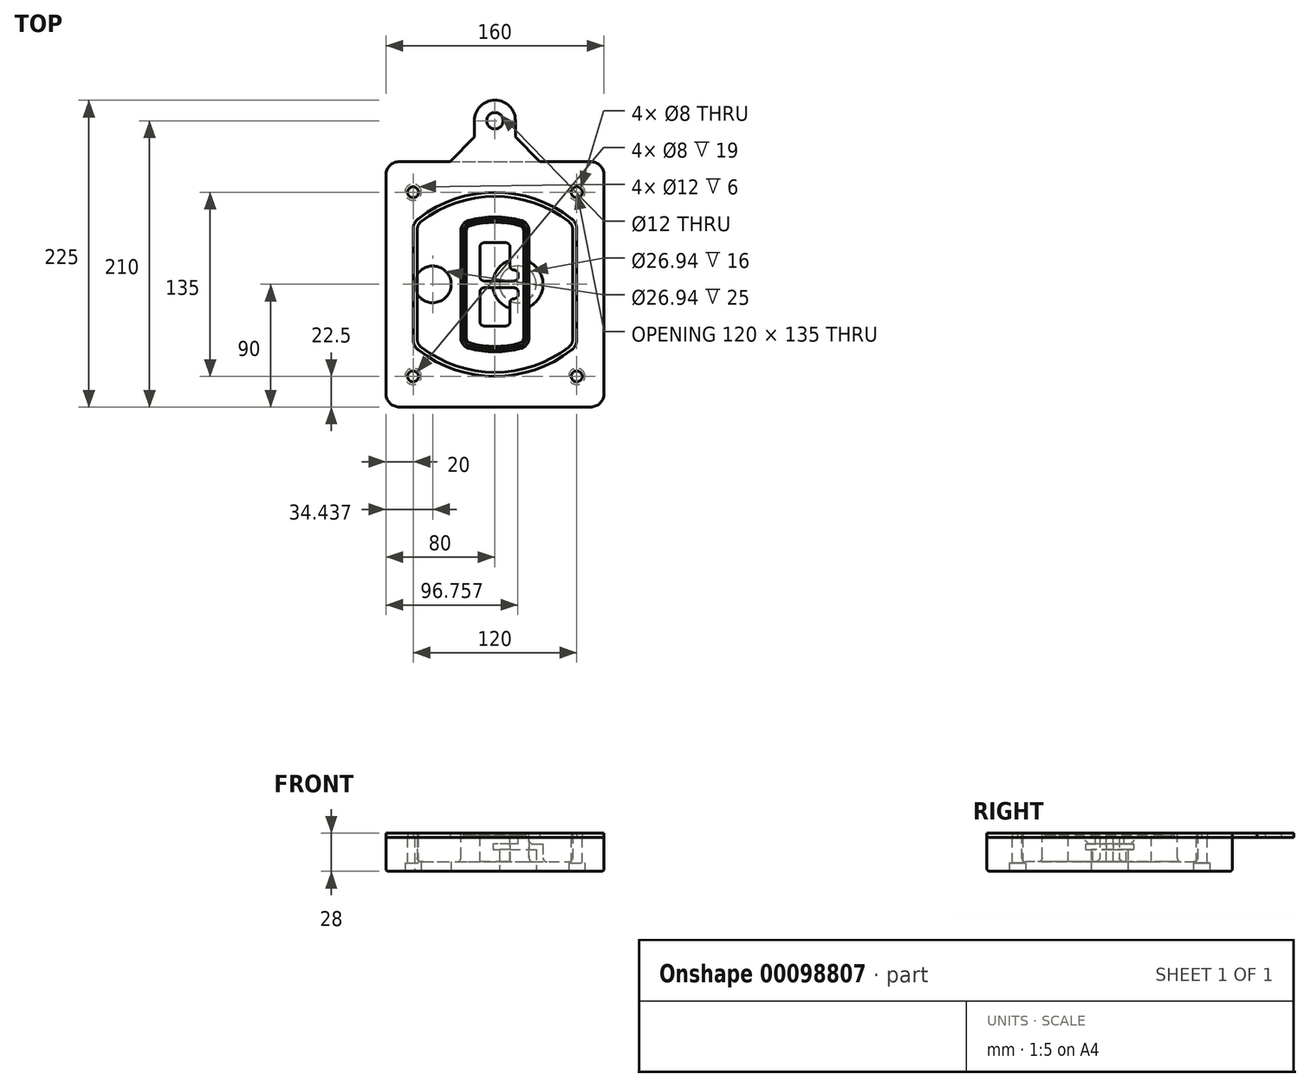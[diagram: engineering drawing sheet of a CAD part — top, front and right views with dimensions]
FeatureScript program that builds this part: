
annotation { "Feature Type Name" : "Feature", "Feature Type Description" : "" }
export const myFeature = defineFeature(function(context is Context, id is Id, definition is map)
    precondition{}
    {
        {
            var Q0;
            Q0=qCreatedBy(makeId("Top.planeOp"),FACE);
            var sketch = newSketch(context, id + "F0", { "sketchPlane" : qUnion([Q0])});
            skPoint(sketch, "E0.rect.middle", {"position": v(0, 0) * mm});
            skLineSegment(sketch, "E1.bottom", {"start": v(-70, -90) * mm, "end": v(70, -90) * mm});
            skLineSegment(sketch, "E1.top", {"start": v(-70, 90) * mm, "end": v(70, 90) * mm});
            skLineSegment(sketch, "E1.left", {"start": v(-80, -80) * mm, "end": v(-80, 80) * mm});
            skLineSegment(sketch, "E1.right", {"start": v(80, -80) * mm, "end": v(80, 80) * mm});
            skLineSegment(sketch, "E2", {"start": v(-80, 90) * mm, "end": v(80, -90) * mm, "construction": true});
            skLineSegment(sketch, "E3", {"start": v(80, 90) * mm, "end": v(-80, -90) * mm, "construction": true});
            skCircle(sketch, "E4", {"center": v(-60, 67.5) * mm, "radius": 4 * mm});
            skCircle(sketch, "E5", {"center": v(60, 67.5) * mm, "radius": 4 * mm});
            skCircle(sketch, "E6", {"center": v(60, -67.5) * mm, "radius": 4 * mm});
            skCircle(sketch, "E7", {"center": v(-60, -67.5) * mm, "radius": 4 * mm});
            skLineSegment(sketch, "E8", {"start": v(-60, 67.5) * mm, "end": v(60, 67.5) * mm, "construction": true});
            skLineSegment(sketch, "E9", {"start": v(60, 67.5) * mm, "end": v(60, -67.5) * mm, "construction": true});
            skLineSegment(sketch, "E10", {"start": v(60, -67.5) * mm, "end": v(-60, -67.5) * mm, "construction": true});
            skLineSegment(sketch, "E11", {"start": v(-60, -67.5) * mm, "end": v(-60, 67.5) * mm, "construction": true});
            skLineSegment(sketch, "E12", {"start": v(-60, 40.3) * mm, "end": v(-60, -40.3) * mm});
            skLineSegment(sketch, "E13", {"start": v(60, 40.3) * mm, "end": v(60, -40.3) * mm});
            skArc(sketch, "E14", {"start": v(56.15, 48.18) * mm, "mid": v(0, 67.5) * mm, "end": v(-56.15, 48.18) * mm});
            skArc(sketch, "E15", {"start": v(-56.15, -48.18) * mm, "mid": v(0, -67.5) * mm, "end": v(56.15, -48.18) * mm});
            skLineSegment(sketch, "E16", {"start": v(-60, 0) * mm, "end": v(60, 0) * mm, "construction": true});
            skPoint(sketch, "E17.visualSharp", {"position": v(-60, -45) * mm});
            skArc(sketch, "E17.filletArc", {"start": v(-60, -40.3) * mm, "mid": v(-58.99, -44.68) * mm, "end": v(-56.15, -48.18) * mm});
            skPoint(sketch, "E18.visualSharp", {"position": v(-60, 45) * mm});
            skArc(sketch, "E18.filletArc", {"start": v(-56.15, 48.18) * mm, "mid": v(-58.99, 44.68) * mm, "end": v(-60, 40.3) * mm});
            skPoint(sketch, "E19.visualSharp", {"position": v(60, 45) * mm});
            skArc(sketch, "E19.filletArc", {"start": v(60, 40.3) * mm, "mid": v(58.99, 44.68) * mm, "end": v(56.15, 48.18) * mm});
            skPoint(sketch, "E20.visualSharp", {"position": v(60, -45) * mm});
            skArc(sketch, "E20.filletArc", {"start": v(56.15, -48.18) * mm, "mid": v(58.99, -44.68) * mm, "end": v(60, -40.3) * mm});
            skPoint(sketch, "E21.visualSharp", {"position": v(-80, 90) * mm});
            skArc(sketch, "E21.filletArc", {"start": v(-70, 90) * mm, "mid": v(-77.07, 87.07) * mm, "end": v(-80, 80) * mm});
            skPoint(sketch, "E22.visualSharp", {"position": v(80, 90) * mm});
            skArc(sketch, "E22.filletArc", {"start": v(80, 80) * mm, "mid": v(77.07, 87.07) * mm, "end": v(70, 90) * mm});
            skPoint(sketch, "E23.visualSharp", {"position": v(80, -90) * mm});
            skArc(sketch, "E23.filletArc", {"start": v(70, -90) * mm, "mid": v(77.07, -87.07) * mm, "end": v(80, -80) * mm});
            skPoint(sketch, "E24.visualSharp", {"position": v(-80, -90) * mm});
            skArc(sketch, "E24.filletArc", {"start": v(-80, -80) * mm, "mid": v(-77.07, -87.07) * mm, "end": v(-70, -90) * mm});
            skArc(sketch, "E25.0", {"start": v(57, 40.3) * mm, "mid": v(56.3, 43.36) * mm, "end": v(54.3, 45.81) * mm});
            skLineSegment(sketch, "E25.1", {"start": v(57, 40.3) * mm, "end": v(57, -40.3) * mm});
            skArc(sketch, "E25.2", {"start": v(54.3, -45.81) * mm, "mid": v(56.3, -43.36) * mm, "end": v(57, -40.3) * mm});
            skArc(sketch, "E25.3", {"start": v(-54.3, -45.81) * mm, "mid": v(0, -64.5) * mm, "end": v(54.3, -45.81) * mm});
            skArc(sketch, "E25.4", {"start": v(-57, -40.3) * mm, "mid": v(-56.3, -43.36) * mm, "end": v(-54.3, -45.81) * mm});
            skArc(sketch, "E25.5", {"start": v(54.3, 45.81) * mm, "mid": v(0, 64.5) * mm, "end": v(-54.3, 45.81) * mm});
            skLineSegment(sketch, "E25.6", {"start": v(-57, 40.3) * mm, "end": v(-57, -40.3) * mm});
            skArc(sketch, "E25.7", {"start": v(-54.3, 45.81) * mm, "mid": v(-56.3, 43.36) * mm, "end": v(-57, 40.3) * mm});
            skArc(sketch, "E26.0", {"start": v(-58.62, 51.33) * mm, "mid": v(-62.58, 46.43) * mm, "end": v(-64, 40.3) * mm});
            skArc(sketch, "E26.1", {"start": v(58.62, 51.33) * mm, "mid": v(0, 71.5) * mm, "end": v(-58.62, 51.33) * mm});
            skArc(sketch, "E26.2", {"start": v(64, 40.3) * mm, "mid": v(62.58, 46.43) * mm, "end": v(58.62, 51.33) * mm});
            skLineSegment(sketch, "E26.3", {"start": v(64, 40.3) * mm, "end": v(64, -40.3) * mm});
            skArc(sketch, "E26.4", {"start": v(58.62, -51.33) * mm, "mid": v(62.58, -46.43) * mm, "end": v(64, -40.3) * mm});
            skLineSegment(sketch, "E26.5", {"start": v(-64, 40.3) * mm, "end": v(-64, -40.3) * mm});
            skArc(sketch, "E26.6", {"start": v(-58.62, -51.33) * mm, "mid": v(0, -71.5) * mm, "end": v(58.62, -51.33) * mm});
            skArc(sketch, "E26.7", {"start": v(-64, -40.3) * mm, "mid": v(-62.58, -46.43) * mm, "end": v(-58.62, -51.33) * mm});
            skSolve(sketch);
        }
        {
            var Q0;
            Q0=makeQuery(id+"F0.imprint","IMPRINT",FACE,{"disambiguationData":[TD([[makeQuery(id+"F0.imprint","IMPRINT",EDGE,{"derivedFrom":sQuery(id+"F0.wireOp",EDGE,"E1.bottom")}),1.0]])]});
            var Q1;
            Q1=makeQuery(id+"F0.imprint","IMPRINT",FACE,{"disambiguationData":[TD([[makeQuery(id+"F0.imprint","IMPRINT",EDGE,{"derivedFrom":sQuery(id+"F0.wireOp",EDGE,"E12")}),1.0]])]});
            var Q2;
            Q2=makeQuery(id+"F0.imprint","IMPRINT",FACE,{"disambiguationData":[TD([[makeQuery(id+"F0.imprint","IMPRINT",EDGE,{"derivedFrom":sQuery(id+"F0.wireOp",EDGE,"E25.0")}),1.0]])]});
            var Q3;
            Q3=makeQuery(id+"F0.imprint","IMPRINT",FACE,{"disambiguationData":[TD([[makeQuery(id+"F0.imprint","IMPRINT",EDGE,{"derivedFrom":sQuery(id+"F0.wireOp",EDGE,"E12")}),-1.0]])]});
            extrude(context, id + "F1", {"entities" : qUnion([Q0, Q1, Q2, Q3]), "oppositeDirection" : true, "depth" : 25 * mm});
        }
        {
            var Q0;
            Q0=makeQuery(id+"F0.imprint","IMPRINT",FACE,{"disambiguationData":[TD([[makeQuery(id+"F0.imprint","IMPRINT",EDGE,{"derivedFrom":sQuery(id+"F0.wireOp",EDGE,"E12")}),1.0]])]});
            extrude(context, id + "F2", {"entities" : qUnion([Q0]), "operationType" : NewBodyOperationType.ADD, "depth" : 3 * mm});
        }
        {
            var Q0;
            Q0=makeQuery(id+"F0.imprint","IMPRINT",FACE,{"disambiguationData":[TD([[makeQuery(id+"F0.imprint","IMPRINT",EDGE,{"derivedFrom":sQuery(id+"F0.wireOp",EDGE,"E25.0")}),1.0]])]});
            extrude(context, id + "F3", {"entities" : qUnion([Q0]), "operationType" : NewBodyOperationType.REMOVE, "oppositeDirection" : true, "depth" : 18 * mm});
        }
        {
            var Q0;
            Q0=makeQuery(id+"F2.opExtrude","CAP_FACE",FACE,{"disambiguationData":[OSD([sQuery(id+"F0.wireOp",EDGE,"E12"),sQuery(id+"F0.wireOp",EDGE,"E13"),sQuery(id+"F0.wireOp",EDGE,"E14"),sQuery(id+"F0.wireOp",EDGE,"E15"),sQuery(id+"F0.wireOp",EDGE,"E17.filletArc"),sQuery(id+"F0.wireOp",EDGE,"E18.filletArc"),sQuery(id+"F0.wireOp",EDGE,"E19.filletArc"),sQuery(id+"F0.wireOp",EDGE,"E20.filletArc"),sQuery(id+"F0.wireOp",EDGE,"E25.0"),sQuery(id+"F0.wireOp",EDGE,"E25.1"),sQuery(id+"F0.wireOp",EDGE,"E25.2"),sQuery(id+"F0.wireOp",EDGE,"E25.3"),sQuery(id+"F0.wireOp",EDGE,"E25.4"),sQuery(id+"F0.wireOp",EDGE,"E25.5"),sQuery(id+"F0.wireOp",EDGE,"E25.6"),sQuery(id+"F0.wireOp",EDGE,"E25.7")])],"isStart":false});
            var sketch = newSketch(context, id + "F4", { "sketchPlane" : qUnion([Q0])});
            skArc(sketch, "E27.0", {"start": v(-19.08, -46.97) * mm, "mid": v(0, -49.5) * mm, "end": v(19.08, -46.97) * mm});
            skArc(sketch, "E28.0", {"start": v(19.08, 46.97) * mm, "mid": v(0, 49.5) * mm, "end": v(-19.08, 46.97) * mm});
            skLineSegment(sketch, "E29", {"start": v(-25, 39.25) * mm, "end": v(-25, -39.25) * mm});
            skLineSegment(sketch, "E30", {"start": v(25, 39.25) * mm, "end": v(25, -39.25) * mm});
            skLineSegment(sketch, "E31", {"start": v(-25, 45.1) * mm, "end": v(25, 45.1) * mm, "construction": true});
            skLineSegment(sketch, "E32", {"start": v(-25, -45.1) * mm, "end": v(25, -45.1) * mm, "construction": true});
            skPoint(sketch, "E33.visualSharp", {"position": v(-25, 45.1) * mm});
            skArc(sketch, "E33.filletArc", {"start": v(-19.08, 46.97) * mm, "mid": v(-23.35, 44.11) * mm, "end": v(-25, 39.25) * mm});
            skPoint(sketch, "E34.visualSharp", {"position": v(25, 45.1) * mm});
            skArc(sketch, "E34.filletArc", {"start": v(25, 39.25) * mm, "mid": v(23.35, 44.11) * mm, "end": v(19.08, 46.97) * mm});
            skPoint(sketch, "E35.visualSharp", {"position": v(25, -45.1) * mm});
            skArc(sketch, "E35.filletArc", {"start": v(19.08, -46.97) * mm, "mid": v(23.35, -44.11) * mm, "end": v(25, -39.25) * mm});
            skPoint(sketch, "E36.visualSharp", {"position": v(-25, -45.1) * mm});
            skArc(sketch, "E36.filletArc", {"start": v(-25, -39.25) * mm, "mid": v(-23.35, -44.11) * mm, "end": v(-19.08, -46.97) * mm});
            skArc(sketch, "E37.0", {"start": v(54.3, 45.81) * mm, "mid": v(0, 64.5) * mm, "end": v(-54.3, 45.81) * mm});
            skArc(sketch, "E37.1", {"start": v(-54.3, 45.81) * mm, "mid": v(-56.3, 43.36) * mm, "end": v(-57, 40.3) * mm});
            skLineSegment(sketch, "E37.2", {"start": v(-57, 40.3) * mm, "end": v(-57, -40.3) * mm});
            skArc(sketch, "E37.3", {"start": v(-57, -40.3) * mm, "mid": v(-56.3, -43.36) * mm, "end": v(-54.3, -45.81) * mm});
            skArc(sketch, "E37.4", {"start": v(-54.3, -45.81) * mm, "mid": v(0, -64.5) * mm, "end": v(54.3, -45.81) * mm});
            skArc(sketch, "E37.5", {"start": v(54.3, -45.81) * mm, "mid": v(56.3, -43.36) * mm, "end": v(57, -40.3) * mm});
            skLineSegment(sketch, "E37.6", {"start": v(57, 40.3) * mm, "end": v(57, -40.3) * mm});
            skArc(sketch, "E37.7", {"start": v(57, 40.3) * mm, "mid": v(56.3, 43.36) * mm, "end": v(54.3, 45.81) * mm});
            skLineSegment(sketch, "E38.0", {"start": v(23, 39.25) * mm, "end": v(23, -39.25) * mm});
            skArc(sketch, "E38.1", {"start": v(18.56, -45.04) * mm, "mid": v(21.76, -42.9) * mm, "end": v(23, -39.25) * mm});
            skArc(sketch, "E38.2", {"start": v(-18.56, -45.04) * mm, "mid": v(0, -47.5) * mm, "end": v(18.56, -45.04) * mm});
            skArc(sketch, "E38.3", {"start": v(-23, -39.25) * mm, "mid": v(-21.76, -42.9) * mm, "end": v(-18.56, -45.04) * mm});
            skLineSegment(sketch, "E38.4", {"start": v(-23, 39.25) * mm, "end": v(-23, -39.25) * mm});
            skArc(sketch, "E38.5", {"start": v(23, 39.25) * mm, "mid": v(21.76, 42.9) * mm, "end": v(18.56, 45.04) * mm});
            skArc(sketch, "E38.6", {"start": v(-18.56, 45.04) * mm, "mid": v(-21.76, 42.9) * mm, "end": v(-23, 39.25) * mm});
            skArc(sketch, "E38.7", {"start": v(18.56, 45.04) * mm, "mid": v(0, 47.5) * mm, "end": v(-18.56, 45.04) * mm});
            skArc(sketch, "E39.0", {"start": v(21, 39.25) * mm, "mid": v(20.18, 41.68) * mm, "end": v(18.04, 43.1) * mm});
            skLineSegment(sketch, "E39.1", {"start": v(21, 39.25) * mm, "end": v(21, -39.25) * mm});
            skArc(sketch, "E39.2", {"start": v(18.04, -43.1) * mm, "mid": v(20.18, -41.68) * mm, "end": v(21, -39.25) * mm});
            skArc(sketch, "E39.3", {"start": v(-18.04, -43.1) * mm, "mid": v(0, -45.5) * mm, "end": v(18.04, -43.1) * mm});
            skArc(sketch, "E39.4", {"start": v(-21, -39.25) * mm, "mid": v(-20.18, -41.68) * mm, "end": v(-18.04, -43.1) * mm});
            skArc(sketch, "E39.5", {"start": v(18.04, 43.1) * mm, "mid": v(0, 45.5) * mm, "end": v(-18.04, 43.1) * mm});
            skLineSegment(sketch, "E39.6", {"start": v(-21, 39.25) * mm, "end": v(-21, -39.25) * mm});
            skArc(sketch, "E39.7", {"start": v(-18.04, 43.1) * mm, "mid": v(-20.18, 41.68) * mm, "end": v(-21, 39.25) * mm});
            skLineSegment(sketch, "E40", {"start": v(-25, 0) * mm, "end": v(25, 0) * mm, "construction": true});
            skLineSegment(sketch, "E41", {"start": v(-11, 5.5) * mm, "end": v(-11, 27.5) * mm});
            skLineSegment(sketch, "E42", {"start": v(-8, 30.5) * mm, "end": v(8, 30.5) * mm});
            skLineSegment(sketch, "E43", {"start": v(11, 27.5) * mm, "end": v(11, 13.5) * mm});
            skLineSegment(sketch, "E44", {"start": v(14, 10.5) * mm, "end": v(14, 10.5) * mm});
            skLineSegment(sketch, "E45", {"start": v(17, 7.5) * mm, "end": v(17, 5.5) * mm});
            skLineSegment(sketch, "E46", {"start": v(14, 2.5) * mm, "end": v(-8, 2.5) * mm});
            skPoint(sketch, "E47.visualSharp", {"position": v(-11, 30.5) * mm});
            skArc(sketch, "E47.filletArc", {"start": v(-8, 30.5) * mm, "mid": v(-10.12, 29.62) * mm, "end": v(-11, 27.5) * mm});
            skPoint(sketch, "E48.visualSharp", {"position": v(11, 30.5) * mm});
            skArc(sketch, "E48.filletArc", {"start": v(11, 27.5) * mm, "mid": v(10.12, 29.62) * mm, "end": v(8, 30.5) * mm});
            skPoint(sketch, "E49.visualSharp", {"position": v(11, 10.5) * mm});
            skArc(sketch, "E49.filletArc", {"start": v(11, 13.5) * mm, "mid": v(11.88, 11.38) * mm, "end": v(14, 10.5) * mm});
            skPoint(sketch, "E50.visualSharp", {"position": v(17, 10.5) * mm});
            skArc(sketch, "E50.filletArc", {"start": v(17, 7.5) * mm, "mid": v(16.12, 9.62) * mm, "end": v(14, 10.5) * mm});
            skPoint(sketch, "E51.visualSharp", {"position": v(17, 2.5) * mm});
            skArc(sketch, "E51.filletArc", {"start": v(14, 2.5) * mm, "mid": v(16.12, 3.38) * mm, "end": v(17, 5.5) * mm});
            skPoint(sketch, "E52.visualSharp", {"position": v(-11, 2.5) * mm});
            skArc(sketch, "E52.filletArc", {"start": v(-11, 5.5) * mm, "mid": v(-10.12, 3.38) * mm, "end": v(-8, 2.5) * mm});
            skLineSegment(sketch, "E53.0.MirrorCS", {"start": v(14, -2.5) * mm, "end": v(-8, -2.5) * mm});
            skArc(sketch, "E54.0.MirrorCS", {"start": v(-11, -5.5) * mm, "mid": v(-10.12, -3.38) * mm, "end": v(-8, -2.5) * mm});
            skLineSegment(sketch, "E55.0.MirrorCS", {"start": v(-11, -5.5) * mm, "end": v(-11, -27.5) * mm});
            skArc(sketch, "E56.0.MirrorCS", {"start": v(-8, -30.5) * mm, "mid": v(-10.12, -29.62) * mm, "end": v(-11, -27.5) * mm});
            skLineSegment(sketch, "E57.0.MirrorCS", {"start": v(-8, -30.5) * mm, "end": v(8, -30.5) * mm});
            skArc(sketch, "E58.0.MirrorCS", {"start": v(11, -27.5) * mm, "mid": v(10.12, -29.62) * mm, "end": v(8, -30.5) * mm});
            skLineSegment(sketch, "E59.0.MirrorCS", {"start": v(11, -27.5) * mm, "end": v(11, -13.5) * mm});
            skArc(sketch, "E60.0.MirrorCS", {"start": v(11, -13.5) * mm, "mid": v(11.88, -11.38) * mm, "end": v(14, -10.5) * mm});
            skArc(sketch, "E61.0.MirrorCS", {"start": v(17, -7.5) * mm, "mid": v(16.12, -9.62) * mm, "end": v(14, -10.5) * mm});
            skLineSegment(sketch, "E62.0.MirrorCS", {"start": v(17, -7.5) * mm, "end": v(17, -5.5) * mm});
            skArc(sketch, "E63.0.MirrorCS", {"start": v(14, -2.5) * mm, "mid": v(16.12, -3.38) * mm, "end": v(17, -5.5) * mm});
            skSolve(sketch);
        }
        {
            var Q0;
            Q0=makeQuery(id+"F4.imprint","IMPRINT",FACE,{"disambiguationData":[TD([[makeQuery(id+"F4.imprint","IMPRINT",EDGE,{"derivedFrom":sQuery(id+"F4.wireOp",EDGE,"E27.0")}),1.0]])]});
            var Q1;
            Q1=makeQuery(id+"F4.imprint","IMPRINT",FACE,{"disambiguationData":[TD([[makeQuery(id+"F4.imprint","IMPRINT",EDGE,{"derivedFrom":sQuery(id+"F4.wireOp",EDGE,"E38.0")}),-1.0]])]});
            var Q2;
            Q2=makeQuery(id+"F4.imprint","IMPRINT",FACE,{"disambiguationData":[TD([[makeQuery(id+"F4.imprint","IMPRINT",EDGE,{"derivedFrom":sQuery(id+"F4.wireOp",EDGE,"E39.0")}),1.0]])]});
            extrude(context, id + "F5", {"entities" : qUnion([Q0, Q1, Q2]), "operationType" : NewBodyOperationType.ADD, "endBound" : BoundingType.UP_TO_NEXT, "oppositeDirection" : true, "depth" : 25 * mm});
        }
        {
            var Q0;
            Q0=makeQuery(id+"F4.imprint","IMPRINT",FACE,{"disambiguationData":[TD([[makeQuery(id+"F4.imprint","IMPRINT",EDGE,{"derivedFrom":sQuery(id+"F4.wireOp",EDGE,"E38.0")}),-1.0]])]});
            extrude(context, id + "F6", {"entities" : qUnion([Q0]), "operationType" : NewBodyOperationType.REMOVE, "oppositeDirection" : true, "depth" : 2 * mm});
        }
        {
            var Q0;
            Q0=makeQuery(id+"F1.opExtrude","CAP_FACE",FACE,{"disambiguationData":[OSD([sQuery(id+"F0.wireOp",EDGE,"E1.bottom"),sQuery(id+"F0.wireOp",EDGE,"E1.top"),sQuery(id+"F0.wireOp",EDGE,"E1.left"),sQuery(id+"F0.wireOp",EDGE,"E1.right"),sQuery(id+"F0.wireOp",EDGE,"E4"),sQuery(id+"F0.wireOp",EDGE,"E5"),sQuery(id+"F0.wireOp",EDGE,"E6"),sQuery(id+"F0.wireOp",EDGE,"E7"),sQuery(id+"F0.wireOp",EDGE,"E21.filletArc"),sQuery(id+"F0.wireOp",EDGE,"E22.filletArc"),sQuery(id+"F0.wireOp",EDGE,"E23.filletArc"),sQuery(id+"F0.wireOp",EDGE,"E24.filletArc")])],"isStart":false});
            var sketch = newSketch(context, id + "F7", { "sketchPlane" : qUnion([Q0])});
            skCircle(sketch, "E64", {"center": v(16.76, 0) * mm, "radius": 13.47 * mm});
            skCircle(sketch, "E65", {"center": v(-45.56, 0) * mm, "radius": 13.47 * mm});
            skLineSegment(sketch, "E66", {"start": v(80, 0) * mm, "end": v(-80, 0) * mm});
            skCircle(sketch, "E67", {"center": v(16.76, 0) * mm, "radius": 18.47 * mm});
            skCircle(sketch, "E68", {"center": v(60, -67.5) * mm, "radius": 6 * mm});
            skCircle(sketch, "E69", {"center": v(-60, -67.5) * mm, "radius": 6 * mm});
            skCircle(sketch, "E70", {"center": v(-60, 67.5) * mm, "radius": 6 * mm});
            skCircle(sketch, "E71", {"center": v(60, 67.5) * mm, "radius": 6 * mm});
            skSolve(sketch);
        }
        {
            var Q0;
            {var subQ1=sQuery(id+"F7.wireOp",EDGE,"E66");var subQ4=sQuery(id+"F7.wireOp",EDGE,"E64");var subQ6=makeQuery(id+"F7.imprint","INTERSECT",VERTEX,{"disambiguationData":[OD(0.0)],"derivedFrom":[subQ4,subQ1]});Q0=makeQuery(id+"F7.imprint","IMPRINT",FACE,{"disambiguationData":[TD([[makeQuery(id+"F7.imprint","IMPRINT",EDGE,{"disambiguationData":[TD([[subQ6,-1.0]])],"derivedFrom":subQ4}),-1.0]])]});}
            var Q1;
            {var subQ0=sQuery(id+"F7.wireOp",EDGE,"E66");var subQ1=sQuery(id+"F7.wireOp",EDGE,"E64");var subQ3=makeQuery(id+"F7.imprint","INTERSECT",VERTEX,{"disambiguationData":[OD(0.0)],"derivedFrom":[subQ1,subQ0]});Q1=makeQuery(id+"F7.imprint","IMPRINT",FACE,{"disambiguationData":[TD([[makeQuery(id+"F7.imprint","IMPRINT",EDGE,{"disambiguationData":[TD([[subQ3,-1.0]])],"derivedFrom":subQ1}),1.0]])]});}
            var Q2;
            {var subQ0=sQuery(id+"F7.wireOp",EDGE,"E66");var subQ1=sQuery(id+"F7.wireOp",EDGE,"E64");var subQ3=makeQuery(id+"F7.imprint","INTERSECT",VERTEX,{"disambiguationData":[OD(0.0)],"derivedFrom":[subQ1,subQ0]});Q2=makeQuery(id+"F7.imprint","IMPRINT",FACE,{"disambiguationData":[TD([[makeQuery(id+"F7.imprint","IMPRINT",EDGE,{"disambiguationData":[TD([[subQ3,1.0]])],"derivedFrom":subQ1}),1.0]])]});}
            var Q3;
            {var subQ1=sQuery(id+"F7.wireOp",EDGE,"E66");var subQ4=sQuery(id+"F7.wireOp",EDGE,"E64");var subQ6=makeQuery(id+"F7.imprint","INTERSECT",VERTEX,{"disambiguationData":[OD(0.0)],"derivedFrom":[subQ4,subQ1]});Q3=makeQuery(id+"F7.imprint","IMPRINT",FACE,{"disambiguationData":[TD([[makeQuery(id+"F7.imprint","IMPRINT",EDGE,{"disambiguationData":[TD([[subQ6,1.0]])],"derivedFrom":subQ4}),-1.0]])]});}
            extrude(context, id + "F8", {"entities" : qUnion([Q0, Q1, Q2, Q3]), "operationType" : NewBodyOperationType.ADD, "oppositeDirection" : true, "depth" : 20 * mm});
        }
        {
            var Q0;
            {var subQ0=sQuery(id+"F7.wireOp",EDGE,"E66");var subQ1=sQuery(id+"F7.wireOp",EDGE,"E64");var subQ3=makeQuery(id+"F7.imprint","INTERSECT",VERTEX,{"disambiguationData":[OD(0.0)],"derivedFrom":[subQ1,subQ0]});Q0=makeQuery(id+"F7.imprint","IMPRINT",FACE,{"disambiguationData":[TD([[makeQuery(id+"F7.imprint","IMPRINT",EDGE,{"disambiguationData":[TD([[subQ3,-1.0]])],"derivedFrom":subQ1}),1.0]])]});}
            var Q1;
            {var subQ0=sQuery(id+"F7.wireOp",EDGE,"E66");var subQ1=sQuery(id+"F7.wireOp",EDGE,"E64");var subQ3=makeQuery(id+"F7.imprint","INTERSECT",VERTEX,{"disambiguationData":[OD(0.0)],"derivedFrom":[subQ1,subQ0]});Q1=makeQuery(id+"F7.imprint","IMPRINT",FACE,{"disambiguationData":[TD([[makeQuery(id+"F7.imprint","IMPRINT",EDGE,{"disambiguationData":[TD([[subQ3,1.0]])],"derivedFrom":subQ1}),1.0]])]});}
            extrude(context, id + "F9", {"entities" : qUnion([Q0, Q1]), "operationType" : NewBodyOperationType.REMOVE, "oppositeDirection" : true, "depth" : 16 * mm});
        }
        {
            var Q0;
            {var subQ0=sQuery(id+"F7.wireOp",EDGE,"E66");var subQ1=sQuery(id+"F7.wireOp",EDGE,"E65");var subQ3=makeQuery(id+"F7.imprint","INTERSECT",VERTEX,{"disambiguationData":[OD(0.0)],"derivedFrom":[subQ1,subQ0]});Q0=makeQuery(id+"F7.imprint","IMPRINT",FACE,{"disambiguationData":[TD([[makeQuery(id+"F7.imprint","IMPRINT",EDGE,{"disambiguationData":[TD([[subQ3,-1.0]])],"derivedFrom":subQ1}),1.0]])]});}
            var Q1;
            {var subQ0=sQuery(id+"F7.wireOp",EDGE,"E66");var subQ1=sQuery(id+"F7.wireOp",EDGE,"E65");var subQ3=makeQuery(id+"F7.imprint","INTERSECT",VERTEX,{"disambiguationData":[OD(0.0)],"derivedFrom":[subQ1,subQ0]});Q1=makeQuery(id+"F7.imprint","IMPRINT",FACE,{"disambiguationData":[TD([[makeQuery(id+"F7.imprint","IMPRINT",EDGE,{"disambiguationData":[TD([[subQ3,1.0]])],"derivedFrom":subQ1}),1.0]])]});}
            extrude(context, id + "F10", {"entities" : qUnion([Q0, Q1]), "operationType" : NewBodyOperationType.REMOVE, "oppositeDirection" : true, "depth" : 25 * mm});
        }
        {
            var Q0;
            Q0=makeQuery(id+"F7.imprint","IMPRINT",FACE,{"disambiguationData":[TD([[makeQuery(id+"F7.imprint","IMPRINT",EDGE,{"derivedFrom":sQuery(id+"F7.wireOp",EDGE,"E68")}),1.0]])]});
            var Q1;
            Q1=makeQuery(id+"F7.imprint","IMPRINT",FACE,{"disambiguationData":[TD([[makeQuery(id+"F7.imprint","IMPRINT",EDGE,{"derivedFrom":makeQuery(id+"F1.opExtrude","CAP_EDGE",EDGE,{"disambiguationData":[OSD([sQuery(id+"F0.wireOp",EDGE,"E5")])],"isStart":false})}),-1.0]])]});
            var Q2;
            Q2=makeQuery(id+"F7.imprint","IMPRINT",FACE,{"disambiguationData":[TD([[makeQuery(id+"F7.imprint","IMPRINT",EDGE,{"derivedFrom":sQuery(id+"F7.wireOp",EDGE,"E69")}),1.0]])]});
            var Q3;
            Q3=makeQuery(id+"F7.imprint","IMPRINT",FACE,{"disambiguationData":[TD([[makeQuery(id+"F7.imprint","IMPRINT",EDGE,{"derivedFrom":makeQuery(id+"F1.opExtrude","CAP_EDGE",EDGE,{"disambiguationData":[OSD([sQuery(id+"F0.wireOp",EDGE,"E4")])],"isStart":false})}),-1.0]])]});
            var Q4;
            Q4=makeQuery(id+"F7.imprint","IMPRINT",FACE,{"disambiguationData":[TD([[makeQuery(id+"F7.imprint","IMPRINT",EDGE,{"derivedFrom":sQuery(id+"F7.wireOp",EDGE,"E70")}),1.0]])]});
            var Q5;
            Q5=makeQuery(id+"F7.imprint","IMPRINT",FACE,{"disambiguationData":[TD([[makeQuery(id+"F7.imprint","IMPRINT",EDGE,{"derivedFrom":makeQuery(id+"F1.opExtrude","CAP_EDGE",EDGE,{"disambiguationData":[OSD([sQuery(id+"F0.wireOp",EDGE,"E7")])],"isStart":false})}),-1.0]])]});
            var Q6;
            Q6=makeQuery(id+"F7.imprint","IMPRINT",FACE,{"disambiguationData":[TD([[makeQuery(id+"F7.imprint","IMPRINT",EDGE,{"derivedFrom":sQuery(id+"F7.wireOp",EDGE,"E71")}),1.0]])]});
            var Q7;
            Q7=makeQuery(id+"F7.imprint","IMPRINT",FACE,{"disambiguationData":[TD([[makeQuery(id+"F7.imprint","IMPRINT",EDGE,{"derivedFrom":makeQuery(id+"F1.opExtrude","CAP_EDGE",EDGE,{"disambiguationData":[OSD([sQuery(id+"F0.wireOp",EDGE,"E6")])],"isStart":false})}),-1.0]])]});
            extrude(context, id + "F11", {"entities" : qUnion([Q0, Q1, Q2, Q3, Q4, Q5, Q6, Q7]), "operationType" : NewBodyOperationType.REMOVE, "oppositeDirection" : true, "depth" : 6 * mm});
        }
        {
            var Q0;
            Q0=makeQuery(id+"F9.boolean.opBoolean","COPY",FACE,{"derivedFrom":makeQuery(id+"F9.opExtrude","CAP_FACE",FACE,{"disambiguationData":[OSD([sQuery(id+"F7.wireOp",EDGE,"E64")])],"isStart":false})});
            var sketch = newSketch(context, id + "F12", { "sketchPlane" : qUnion([Q0])});
            skArc(sketch, "E72.0", {"start": v(11, 17.55) * mm, "mid": v(2.57, 11.82) * mm, "end": v(-1.54, 2.5) * mm});
            skArc(sketch, "E72.1", {"start": v(-1.54, -2.5) * mm, "mid": v(2.57, -11.82) * mm, "end": v(11, -17.55) * mm});
            skLineSegment(sketch, "E73", {"start": v(-1.54, -2.5) * mm, "end": v(14, -2.5) * mm});
            skLineSegment(sketch, "E74.0", {"start": v(14, 2.5) * mm, "end": v(-1.54, 2.5) * mm});
            skArc(sketch, "E74.1", {"start": v(14, 2.5) * mm, "mid": v(16.12, 3.38) * mm, "end": v(17, 5.5) * mm});
            skLineSegment(sketch, "E74.2", {"start": v(17, 7.5) * mm, "end": v(17, 5.5) * mm});
            skArc(sketch, "E74.3", {"start": v(17, 7.5) * mm, "mid": v(16.12, 9.62) * mm, "end": v(14, 10.5) * mm});
            skArc(sketch, "E74.4", {"start": v(11, 13.5) * mm, "mid": v(11.88, 11.38) * mm, "end": v(14, 10.5) * mm});
            skLineSegment(sketch, "E74.5", {"start": v(11, 17.55) * mm, "end": v(11, 13.5) * mm});
            skLineSegment(sketch, "E74.7", {"start": v(14, -2.5) * mm, "end": v(-1.54, -2.5) * mm});
            skArc(sketch, "E74.8", {"start": v(14, -2.5) * mm, "mid": v(16.12, -3.38) * mm, "end": v(17, -5.5) * mm});
            skLineSegment(sketch, "E74.9", {"start": v(17, -7.5) * mm, "end": v(17, -5.5) * mm});
            skArc(sketch, "E74.10", {"start": v(17, -7.5) * mm, "mid": v(16.12, -9.62) * mm, "end": v(14, -10.5) * mm});
            skArc(sketch, "E74.11", {"start": v(11, -13.5) * mm, "mid": v(11.88, -11.38) * mm, "end": v(14, -10.5) * mm});
            skLineSegment(sketch, "E74.12", {"start": v(11, -17.55) * mm, "end": v(11, -13.5) * mm});
            skPoint(sketch, "E75.orphan", {"position": v(11, -27.5) * mm});
            skPoint(sketch, "E76.orphan", {"position": v(-8, -2.5) * mm});
            skPoint(sketch, "E77.orphan", {"position": v(-8, 2.5) * mm});
            skPoint(sketch, "E78.orphan", {"position": v(11, 27.5) * mm});
            skSolve(sketch);
        }
        {
            var Q0;
            {var subQ7=sQuery(id+"F12.wireOp",EDGE,"E72.0");var subQ14=sQuery(id+"F12.wireOp",EDGE,"E72.1");var subQ16=sQuery(id+"F12.wireOp",EDGE,"E74.1");var subQ18=sQuery(id+"F12.wireOp",EDGE,"E74.8");Q0=qUnion([makeQuery(id+"F12.imprint","IMPRINT",FACE,{"disambiguationData":[TD([[makeQuery(id+"F12.imprint","IMPRINT",EDGE,{"derivedFrom":subQ7}),1.0]])]}),makeQuery(id+"F12.imprint","IMPRINT",FACE,{"disambiguationData":[TD([[makeQuery(id+"F12.imprint","IMPRINT",EDGE,{"derivedFrom":subQ14}),1.0]])]}),makeQuery(id+"F12.imprint","IMPRINT",FACE,{"disambiguationData":[TD([[makeQuery(id+"F12.imprint","IMPRINT",EDGE,{"derivedFrom":subQ16}),1.0]])]}),makeQuery(id+"F12.imprint","IMPRINT",FACE,{"disambiguationData":[TD([[makeQuery(id+"F12.imprint","IMPRINT",EDGE,{"derivedFrom":subQ18}),-1.0]])]})]);}
            var Q1;
            Q1=makeQuery(id+"F5.boolean.opBoolean","SPLIT",FACE,{"disambiguationData":[TD([makeQuery(id+"F5.opExtrude","SWEPT_FACE",FACE,{"disambiguationData":[OSD([sQuery(id+"F4.wireOp",EDGE,"E41")])]})])],"derivedFrom":makeQuery(id+"F3.boolean.opBoolean","COPY",FACE,{"derivedFrom":makeQuery(id+"F3.opExtrude","CAP_FACE",FACE,{"disambiguationData":[OSD([sQuery(id+"F0.wireOp",EDGE,"E25.0"),sQuery(id+"F0.wireOp",EDGE,"E25.1"),sQuery(id+"F0.wireOp",EDGE,"E25.2"),sQuery(id+"F0.wireOp",EDGE,"E25.3"),sQuery(id+"F0.wireOp",EDGE,"E25.4"),sQuery(id+"F0.wireOp",EDGE,"E25.5"),sQuery(id+"F0.wireOp",EDGE,"E25.6"),sQuery(id+"F0.wireOp",EDGE,"E25.7")])],"isStart":false})})});
            extrude(context, id + "F13", {"entities" : qUnion([Q0]), "operationType" : NewBodyOperationType.REMOVE, "endBound" : BoundingType.UP_TO_SURFACE, "endBoundEntityFace" : qUnion([Q1]), "depth" : 25 * mm});
        }
        {
            var Q0;
            Q0=makeQuery(id+"F3.boolean.opBoolean","COPY",EDGE,{"derivedFrom":makeQuery(id+"F3.opExtrude","CAP_EDGE",EDGE,{"disambiguationData":[OSD([sQuery(id+"F0.wireOp",EDGE,"E25.6")])],"isStart":false})});
            var Q1;
            Q1=makeQuery(id+"F8.boolean.opBoolean","INTERSECT",EDGE,{"derivedFrom":[makeQuery(id+"F5.opExtrude","SWEPT_FACE",FACE,{"disambiguationData":[OSD([sQuery(id+"F4.wireOp",EDGE,"E30")])]}),makeQuery(id+"F8.opExtrude","CAP_FACE",FACE,{"disambiguationData":[OSD([sQuery(id+"F7.wireOp",EDGE,"E67")])],"isStart":false})]});
            var Q2;
            Q2=makeQuery(id+"F8.boolean.opBoolean","INTERSECT",EDGE,{"disambiguationData":[OD(1.0)],"derivedFrom":[makeQuery(id+"F5.opExtrude","SWEPT_FACE",FACE,{"disambiguationData":[OSD([sQuery(id+"F4.wireOp",EDGE,"E30")])]}),makeQuery(id+"F8.opExtrude","SWEPT_FACE",FACE,{"disambiguationData":[OSD([sQuery(id+"F7.wireOp",EDGE,"E67")])]})]});
            var Q3;
            {var subQ0=sQuery(id+"F4.wireOp",EDGE,"E30");Q3=makeQuery(id+"F8.boolean.opBoolean","SPLIT",EDGE,{"disambiguationData":[TD([makeQuery(id+"F5.opExtrude","SWEPT_FACE",FACE,{"disambiguationData":[OSD([sQuery(id+"F4.wireOp",EDGE,"E35.filletArc")])]})])],"derivedFrom":makeQuery(id+"F5.opExtrude","CAP_EDGE",EDGE,{"disambiguationData":[OSD([subQ0])],"isStart":false})});}
            var Q4;
            {var subQ0=sQuery(id+"F0.wireOp",EDGE,"E25.7");var subQ1=sQuery(id+"F0.wireOp",EDGE,"E25.1");var subQ2=sQuery(id+"F0.wireOp",EDGE,"E25.6");var subQ3=sQuery(id+"F0.wireOp",EDGE,"E25.5");var subQ4=sQuery(id+"F0.wireOp",EDGE,"E25.4");var subQ5=sQuery(id+"F0.wireOp",EDGE,"E25.0");var subQ6=sQuery(id+"F0.wireOp",EDGE,"E25.2");var subQ7=sQuery(id+"F0.wireOp",EDGE,"E25.3");Q4=makeQuery(id+"F8.boolean.opBoolean","INTERSECT",EDGE,{"derivedFrom":[makeQuery(id+"F5.boolean.opBoolean","SPLIT",FACE,{"disambiguationData":[TD([makeQuery(id+"F2.opExtrude","SWEPT_FACE",FACE,{"disambiguationData":[OSD([subQ5])]})])],"derivedFrom":makeQuery(id+"F3.boolean.opBoolean","COPY",FACE,{"derivedFrom":makeQuery(id+"F3.opExtrude","CAP_FACE",FACE,{"disambiguationData":[OSD([subQ5,subQ1,subQ6,subQ7,subQ4,subQ3,subQ2,subQ0])],"isStart":false})})}),makeQuery(id+"F8.opExtrude","SWEPT_FACE",FACE,{"disambiguationData":[OSD([sQuery(id+"F7.wireOp",EDGE,"E67")])]})]});}
            var Q5;
            Q5=makeQuery(id+"F8.boolean.opBoolean","INTERSECT",EDGE,{"disambiguationData":[OD(0.0)],"derivedFrom":[makeQuery(id+"F5.opExtrude","SWEPT_FACE",FACE,{"disambiguationData":[OSD([sQuery(id+"F4.wireOp",EDGE,"E30")])]}),makeQuery(id+"F8.opExtrude","SWEPT_FACE",FACE,{"disambiguationData":[OSD([sQuery(id+"F7.wireOp",EDGE,"E67")])]})]});
            fillet(context, id + "F14", {"entities" : qUnion([Q0, Q1, Q2, Q3, Q4, Q5]), "radius" : 3 * mm, "tangentPropagation" : true, "allowEdgeOverflow" : false});
        }
        {
            var Q0;
            Q0=makeQuery(id+"F1.opExtrude","CAP_EDGE",EDGE,{"disambiguationData":[OSD([sQuery(id+"F0.wireOp",EDGE,"E1.bottom")])],"isStart":false});
            fillet(context, id + "F15", {"entities" : qUnion([Q0]), "radius" : 2 * mm, "tangentPropagation" : true, "allowEdgeOverflow" : false});
        }
        {
            var Q0;
            {var subQ0=sQuery(id+"F0.wireOp",EDGE,"E22.filletArc");var subQ1=sQuery(id+"F0.wireOp",EDGE,"E7");var subQ2=sQuery(id+"F0.wireOp",EDGE,"E6");var subQ3=sQuery(id+"F0.wireOp",EDGE,"E5");var subQ4=sQuery(id+"F0.wireOp",EDGE,"E4");var subQ5=sQuery(id+"F0.wireOp",EDGE,"E1.bottom");var subQ6=sQuery(id+"F0.wireOp",EDGE,"E21.filletArc");var subQ7=sQuery(id+"F0.wireOp",EDGE,"E1.top");var subQ8=sQuery(id+"F0.wireOp",EDGE,"E1.left");var subQ9=sQuery(id+"F0.wireOp",EDGE,"E1.right");var subQ10=sQuery(id+"F0.wireOp",EDGE,"E23.filletArc");var subQ11=sQuery(id+"F0.wireOp",EDGE,"E24.filletArc");Q0=makeQuery(id+"F2.boolean.opBoolean","SPLIT",FACE,{"disambiguationData":[TD([makeQuery(id+"F1.opExtrude","SWEPT_FACE",FACE,{"disambiguationData":[OSD([subQ5])]})])],"derivedFrom":makeQuery(id+"F1.opExtrude","CAP_FACE",FACE,{"disambiguationData":[OSD([subQ5,subQ7,subQ8,subQ9,subQ4,subQ3,subQ2,subQ1,subQ6,subQ0,subQ10,subQ11])],"isStart":true})});}
            var sketch = newSketch(context, id + "F16", { "sketchPlane" : qUnion([Q0])});
            skArc(sketch, "E79.0", {"start": v(56.15, 48.18) * mm, "mid": v(0, 67.5) * mm, "end": v(-56.15, 48.18) * mm});
            skArc(sketch, "E79.1", {"start": v(-56.15, 48.18) * mm, "mid": v(-58.99, 44.68) * mm, "end": v(-60, 40.3) * mm});
            skLineSegment(sketch, "E79.2", {"start": v(-60, 40.3) * mm, "end": v(-60, -40.3) * mm});
            skArc(sketch, "E79.3", {"start": v(-60, -40.3) * mm, "mid": v(-58.99, -44.68) * mm, "end": v(-56.15, -48.18) * mm});
            skArc(sketch, "E79.4", {"start": v(-56.15, -48.18) * mm, "mid": v(0, -67.5) * mm, "end": v(56.15, -48.18) * mm});
            skArc(sketch, "E79.5", {"start": v(56.15, -48.18) * mm, "mid": v(58.99, -44.68) * mm, "end": v(60, -40.3) * mm});
            skLineSegment(sketch, "E79.6", {"start": v(60, 40.3) * mm, "end": v(60, -40.3) * mm});
            skArc(sketch, "E79.7", {"start": v(60, 40.3) * mm, "mid": v(58.99, 44.68) * mm, "end": v(56.15, 48.18) * mm});
            skLineSegment(sketch, "E79.8", {"start": v(80, -80) * mm, "end": v(80, 80) * mm});
            skArc(sketch, "E79.9", {"start": v(80, 80) * mm, "mid": v(77.07, 87.07) * mm, "end": v(70, 90) * mm});
            skLineSegment(sketch, "E79.10", {"start": v(-70, 90) * mm, "end": v(70, 90) * mm});
            skLineSegment(sketch, "E79.11", {"start": v(-80, -80) * mm, "end": v(-80, 80) * mm});
            skArc(sketch, "E79.12", {"start": v(-80, -80) * mm, "mid": v(-77.07, -87.07) * mm, "end": v(-70, -90) * mm});
            skLineSegment(sketch, "E79.13", {"start": v(-70, -90) * mm, "end": v(70, -90) * mm});
            skArc(sketch, "E79.14", {"start": v(-70, 90) * mm, "mid": v(-77.07, 87.07) * mm, "end": v(-80, 80) * mm});
            skArc(sketch, "E79.15", {"start": v(70, -90) * mm, "mid": v(77.07, -87.07) * mm, "end": v(80, -80) * mm});
            skCircle(sketch, "E79.16", {"center": v(60, 67.5) * mm, "radius": 4 * mm});
            skCircle(sketch, "E79.17", {"center": v(-60, 67.5) * mm, "radius": 4 * mm});
            skCircle(sketch, "E79.18", {"center": v(-60, -67.5) * mm, "radius": 4 * mm});
            skCircle(sketch, "E79.19", {"center": v(60, -67.5) * mm, "radius": 4 * mm});
            skLineSegment(sketch, "E80", {"start": v(0, 90) * mm, "end": v(0, 120) * mm, "construction": true});
            skPoint(sketch, "E80.endSnap0", {"position": v(0, 90) * mm});
            skCircle(sketch, "E81", {"center": v(0, 120) * mm, "radius": 6 * mm});
            skArc(sketch, "E82", {"start": v(15, 120) * mm, "mid": v(0, 135) * mm, "end": v(-15, 120) * mm});
            skLineSegment(sketch, "E83", {"start": v(-15, 108) * mm, "end": v(-33, 90) * mm});
            skLineSegment(sketch, "E84", {"start": v(-15, 120) * mm, "end": v(-15, 108) * mm});
            skLineSegment(sketch, "E85", {"start": v(15, 120) * mm, "end": v(15, 108) * mm});
            skLineSegment(sketch, "E86", {"start": v(15, 108) * mm, "end": v(33, 90) * mm});
            skLineSegment(sketch, "E87", {"start": v(-98.71, 0) * mm, "end": v(98.93, 0) * mm, "construction": true});
            skArc(sketch, "E88.MirrorCS", {"start": v(15, -120) * mm, "mid": v(0, -135) * mm, "end": v(-15, -120) * mm});
            skLineSegment(sketch, "E89.MirrorCS", {"start": v(15, -120) * mm, "end": v(15, -108) * mm});
            skLineSegment(sketch, "E90.MirrorCS", {"start": v(15, -108) * mm, "end": v(33, -90) * mm});
            skLineSegment(sketch, "E91.MirrorCS", {"start": v(-15, -108) * mm, "end": v(-33, -90) * mm});
            skLineSegment(sketch, "E92.MirrorCS", {"start": v(-15, -120) * mm, "end": v(-15, -108) * mm});
            skCircle(sketch, "E93.MirrorC", {"center": v(0, -120) * mm, "radius": 6 * mm});
            skLineSegment(sketch, "E94.MirrorCS", {"start": v(0, -90) * mm, "end": v(0, -120) * mm, "construction": true});
            skSolve(sketch);
        }
        {
            var Q0;
            Q0=makeQuery(id+"F16.imprint","IMPRINT",FACE,{"disambiguationData":[TD([[makeQuery(id+"F16.imprint","IMPRINT",EDGE,{"derivedFrom":sQuery(id+"F16.wireOp",EDGE,"E79.0")}),-1.0]])]});
            var Q1;
            Q1=makeQuery(id+"F16.imprint","IMPRINT",FACE,{"disambiguationData":[TD([[makeQuery(id+"F16.imprint","IMPRINT",EDGE,{"derivedFrom":sQuery(id+"F16.wireOp",EDGE,"E88.MirrorCS")}),-1.0]])]});
            var Q2;
            Q2=makeQuery(id+"F16.imprint","IMPRINT",FACE,{"disambiguationData":[TD([[makeQuery(id+"F16.imprint","IMPRINT",EDGE,{"derivedFrom":sQuery(id+"F16.wireOp",EDGE,"E81")}),-1.0]])]});
            var Q3;
            Q3=makeQuery(id+"F2.opExtrude","CAP_FACE",FACE,{"disambiguationData":[OSD([sQuery(id+"F0.wireOp",EDGE,"E12"),sQuery(id+"F0.wireOp",EDGE,"E13"),sQuery(id+"F0.wireOp",EDGE,"E14"),sQuery(id+"F0.wireOp",EDGE,"E15"),sQuery(id+"F0.wireOp",EDGE,"E17.filletArc"),sQuery(id+"F0.wireOp",EDGE,"E18.filletArc"),sQuery(id+"F0.wireOp",EDGE,"E19.filletArc"),sQuery(id+"F0.wireOp",EDGE,"E20.filletArc"),sQuery(id+"F0.wireOp",EDGE,"E25.0"),sQuery(id+"F0.wireOp",EDGE,"E25.1"),sQuery(id+"F0.wireOp",EDGE,"E25.2"),sQuery(id+"F0.wireOp",EDGE,"E25.3"),sQuery(id+"F0.wireOp",EDGE,"E25.4"),sQuery(id+"F0.wireOp",EDGE,"E25.5"),sQuery(id+"F0.wireOp",EDGE,"E25.6"),sQuery(id+"F0.wireOp",EDGE,"E25.7")])],"isStart":false});
            extrude(context, id + "F17", {"entities" : qUnion([Q0, Q1, Q2]), "endBound" : BoundingType.UP_TO_SURFACE, "endBoundEntityFace" : qUnion([Q3]), "depth" : 25 * mm});
        }
    });
